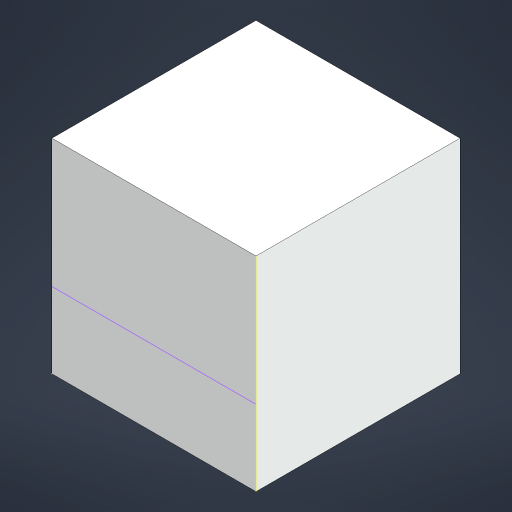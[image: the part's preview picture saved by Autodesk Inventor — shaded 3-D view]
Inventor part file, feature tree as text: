
AUTODESK INVENTOR PART (.ipt)
format: ipt  version: 2023.1 (Build 271208000, 208)  size: 132,608 bytes
history: native  units: in
note: dims shown in document units (in); Inventor stores cm internally (conversion verified against a paired STEP export)
features: sketch x2, extrude x1
ambient origin geometry x8: Origin, YZ Plane, XZ Plane, XY Plane, X Axis, Y Axis, Z Axis, Center Point
bodies: Solid1 (feature_tree)
feature tree (3):
  extrude  "Extrusion1"  Depth=20.0in
  sketch  "Sketch3"  dims[d5=20.0in d6=0.0in]
  sketch  "Sketch2"  dims[d3=20.0in d4=20.0in]
